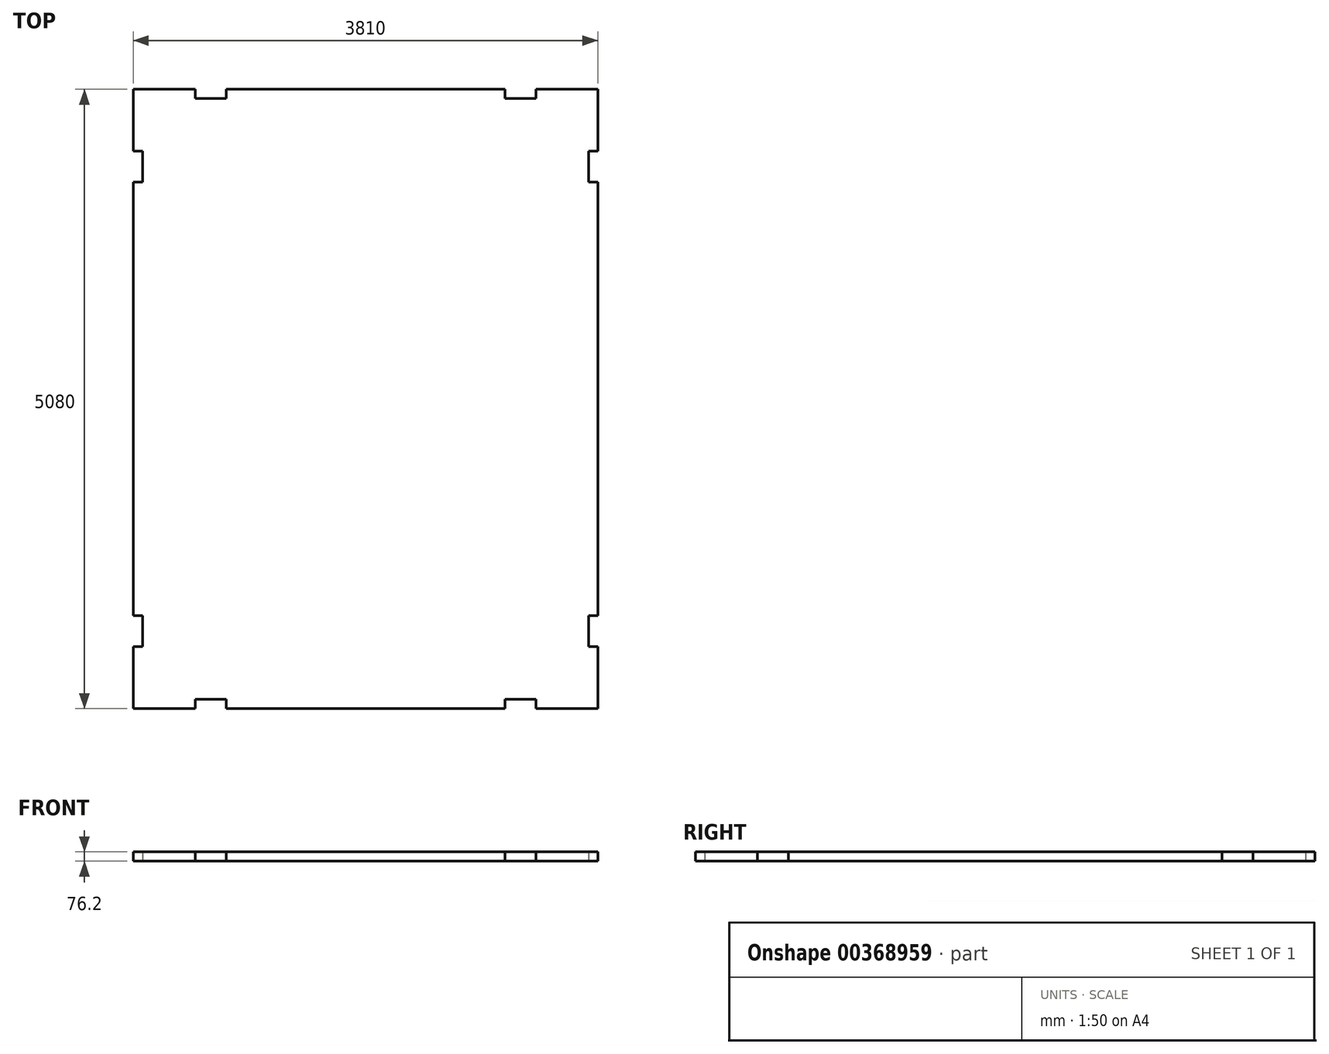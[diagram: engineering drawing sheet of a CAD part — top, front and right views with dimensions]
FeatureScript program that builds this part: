
annotation { "Feature Type Name" : "Feature", "Feature Type Description" : "" }
export const myFeature = defineFeature(function(context is Context, id is Id, definition is map)
    precondition{}
    {
        {
            var Q0;
            Q0=qCreatedBy(makeId("Top.planeOp"),FACE);
            var sketch = newSketch(context, id + "F0", { "sketchPlane" : qUnion([Q0])});
            skLineSegment(sketch, "E0.bottom", {"start": v(1905, 2540) * mm, "end": v(1397, 2540) * mm});
            skLineSegment(sketch, "E0.top", {"start": v(1143, -2540) * mm, "end": v(-1143, -2540) * mm});
            skLineSegment(sketch, "E0.left", {"start": v(1905, 2540) * mm, "end": v(1905, 2032) * mm});
            skLineSegment(sketch, "E0.right", {"start": v(-1905, 2540) * mm, "end": v(-1905, 2032) * mm});
            skPoint(sketch, "E0.middle", {"position": v(0, 0) * mm});
            skLineSegment(sketch, "E1", {"start": v(-1905, 1778) * mm, "end": v(-1828.8, 1778) * mm});
            skLineSegment(sketch, "E2", {"start": v(-1905, 2032) * mm, "end": v(-1828.8, 2032) * mm});
            skLineSegment(sketch, "E3", {"start": v(-1828.8, 2032) * mm, "end": v(-1828.8, 1778) * mm});
            skLineSegment(sketch, "E4.trimOffspring", {"start": v(-1905, 1778) * mm, "end": v(-1905, -1778) * mm});
            skLineSegment(sketch, "E5", {"start": v(-1905, 2540) * mm, "end": v(-1397, 2540) * mm});
            skLineSegment(sketch, "E6", {"start": v(-1397, 2540) * mm, "end": v(-1143, 2540) * mm});
            skLineSegment(sketch, "E7", {"start": v(-1397, 2540) * mm, "end": v(-1397, 2463.8) * mm});
            skLineSegment(sketch, "E8", {"start": v(-1397, 2463.8) * mm, "end": v(-1143, 2463.8) * mm});
            skLineSegment(sketch, "E9", {"start": v(-1143, 2540) * mm, "end": v(-1143, 2463.8) * mm});
            skLineSegment(sketch, "E10", {"start": v(-1905, -2540) * mm, "end": v(-1905, -2032) * mm});
            skLineSegment(sketch, "E11", {"start": v(-1905, -2032) * mm, "end": v(-1828.8, -2032) * mm});
            skLineSegment(sketch, "E12", {"start": v(-1905, -1778) * mm, "end": v(-1828.8, -1778) * mm});
            skLineSegment(sketch, "E13", {"start": v(-1828.8, -1778) * mm, "end": v(-1828.8, -2032) * mm});
            skLineSegment(sketch, "E14", {"start": v(-1905, -2540) * mm, "end": v(-1397, -2540) * mm});
            skLineSegment(sketch, "E15", {"start": v(-1397, -2540) * mm, "end": v(-1397, -2463.8) * mm});
            skLineSegment(sketch, "E16", {"start": v(-1397, -2463.8) * mm, "end": v(-1143, -2463.8) * mm});
            skLineSegment(sketch, "E17", {"start": v(-1143, -2463.8) * mm, "end": v(-1143, -2540) * mm});
            skLineSegment(sketch, "E18.trimOffspring", {"start": v(-1397, -2540) * mm, "end": v(-1905, -2540) * mm});
            skLineSegment(sketch, "E19", {"start": v(1905, -2540) * mm, "end": v(1397, -2540) * mm});
            skLineSegment(sketch, "E20", {"start": v(1397, -2540) * mm, "end": v(1397, -2463.8) * mm});
            skLineSegment(sketch, "E21", {"start": v(1397, -2463.8) * mm, "end": v(1143, -2463.8) * mm});
            skLineSegment(sketch, "E22", {"start": v(1143, -2463.8) * mm, "end": v(1143, -2540) * mm});
            skLineSegment(sketch, "E23", {"start": v(1905, -2540) * mm, "end": v(1905, -2032) * mm});
            skLineSegment(sketch, "E24", {"start": v(1905, -2032) * mm, "end": v(1828.8, -2032) * mm});
            skLineSegment(sketch, "E25", {"start": v(1828.8, -2032) * mm, "end": v(1828.8, -1778) * mm});
            skLineSegment(sketch, "E26", {"start": v(1828.8, -1778) * mm, "end": v(1905, -1778) * mm});
            skLineSegment(sketch, "E27.trimOffspring", {"start": v(1905, -2032) * mm, "end": v(1905, -2540) * mm});
            skLineSegment(sketch, "E28", {"start": v(1905, 2032) * mm, "end": v(1828.8, 2032) * mm});
            skLineSegment(sketch, "E29", {"start": v(1828.8, 2032) * mm, "end": v(1828.8, 1778) * mm});
            skLineSegment(sketch, "E30", {"start": v(1905, 1778) * mm, "end": v(1828.8, 1778) * mm});
            skLineSegment(sketch, "E31.trimOffspring", {"start": v(1905, 1778) * mm, "end": v(1905, -1778) * mm});
            skLineSegment(sketch, "E32", {"start": v(1397, 2540) * mm, "end": v(1397, 2463.8) * mm});
            skLineSegment(sketch, "E33", {"start": v(1143, 2540) * mm, "end": v(1143, 2463.8) * mm});
            skLineSegment(sketch, "E34", {"start": v(1397, 2463.8) * mm, "end": v(1143, 2463.8) * mm});
            skLineSegment(sketch, "E35.trimOffspring", {"start": v(1143, 2540) * mm, "end": v(-1905, 2540) * mm});
            skLineSegment(sketch, "E36.trimOffspring", {"start": v(-1905, -2032) * mm, "end": v(-1905, -2540) * mm});
            skSolve(sketch);
        }
        {
            var Q0;
            Q0=makeQuery(id+"F0.imprint","IMPRINT",FACE,{"disambiguationData":[TD([[makeQuery(id+"F0.imprint","IMPRINT",EDGE,{"derivedFrom":sQuery(id+"F0.wireOp",EDGE,"E0.top")}),-1.0]])]});
            extrude(context, id + "F1", {"entities" : qUnion([Q0]), "depth" : 76.2 * mm});
        }
    });
